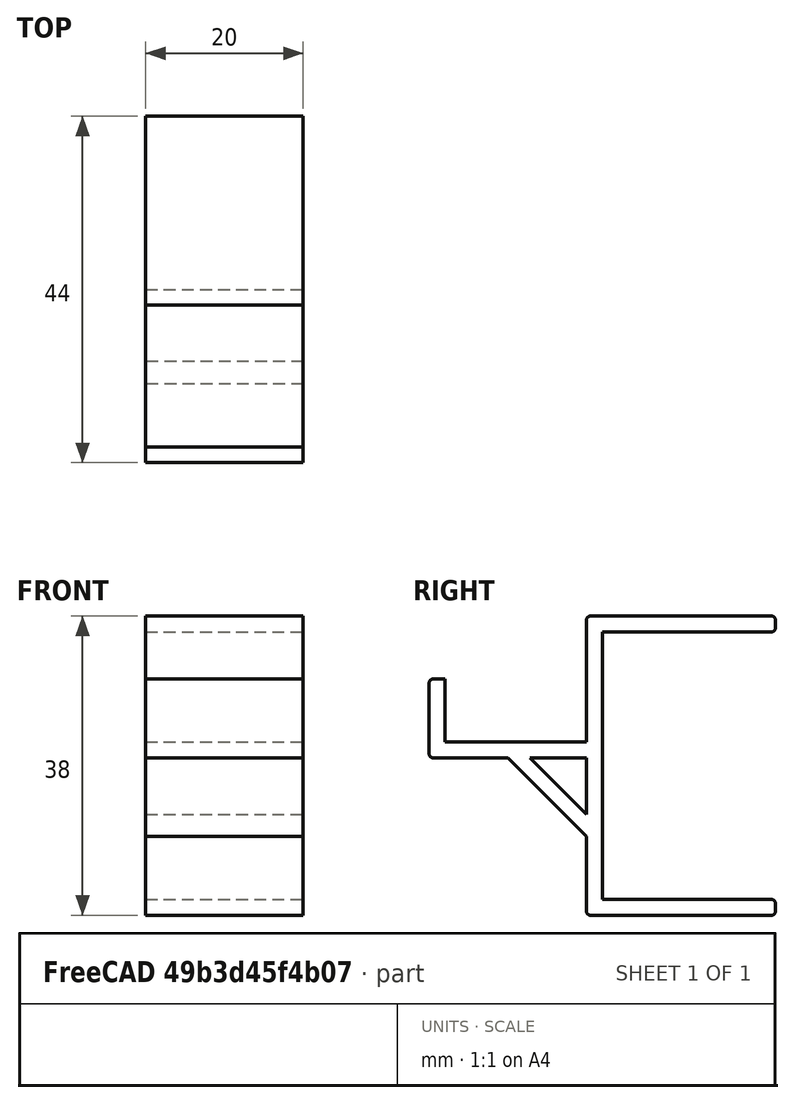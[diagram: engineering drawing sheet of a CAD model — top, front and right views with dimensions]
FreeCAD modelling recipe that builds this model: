
FCSTD DOCUMENT  (FreeCAD 0.17R13541 (Git))
Label: monitor-arm-hanger-wide
License: All rights reserved
LicenseURL: http://en.wikipedia.org/wiki/All_rights_reserved
objects: Part::Box×5, Part::Cut×2, Part::MultiFuse×2, Part::Fillet×1
note: 10 computed .brp shape members not serialized (recipe doc carries the construction recipe); baked Part::Feature solids carry a one-line shape summary decoded from their .brp

FEATURE [Part::Box] Box  label="Cube"
  AttacherType = Attacher::AttachEngine3D
  Height = 38
  Length = 20
  Width = 24
FEATURE [Part::Box] Box001  label="Cube001"
  AttacherType = Attacher::AttachEngine3D
  Height = 34
  Length = 20
  Placement = pos=(0,2,2) rot=(0,0,1;0rad)
  Width = 30
FEATURE [Part::Cut] Cut
  Base = -> Box
  Tool = -> Box001
FEATURE [Part::Box] Box002  label="Cube002"
  AttacherType = Attacher::AttachEngine3D
  Height = 8
  Length = 20
  Placement = pos=(0,-18,22) rot=(0,0,1;0rad)
  Width = 18
FEATURE [Part::Box] Box003  label="Cube003"
  AttacherType = Attacher::AttachEngine3D
  Height = 10
  Length = 20
  Placement = pos=(0,-20,20) rot=(0,0,1;0rad)
  Width = 20
FEATURE [Part::Cut] Cut001
  Base = -> Box003
  Tool = -> Box002
FEATURE [Part::MultiFuse] Fusion
  Shapes = -> [Cut001,Cut]
FEATURE [Part::Box] Box004  label="Cube004"
  AttacherType = Attacher::AttachEngine3D
  Height = 14.5
  Length = 20
  Placement = pos=(0,0,10) rot=(1,0,0;0.785398rad)
  Width = 2
FEATURE [Part::MultiFuse] Fusion001
  Shapes = -> [Fusion,Box004]
FEATURE [Part::Fillet] Fillet
  Base = -> Fusion001
  Edges = 8 edges r=0.5: [Edge4,Edge24,Edge55,Edge56,Edge57,Edge60,Edge61,Edge62]
